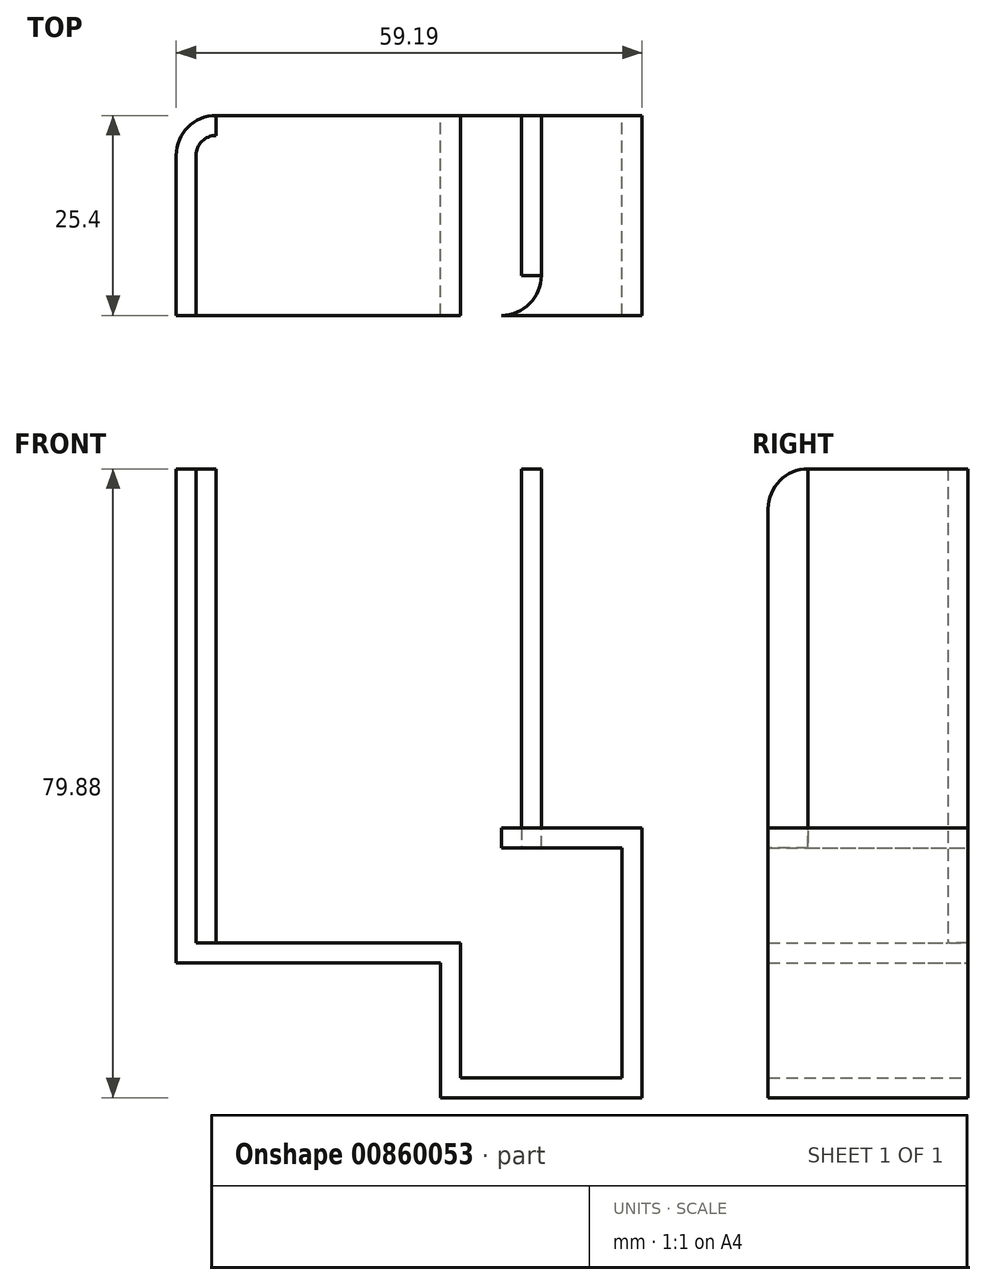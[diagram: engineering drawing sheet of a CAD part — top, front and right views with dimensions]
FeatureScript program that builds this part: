
annotation { "Feature Type Name" : "Feature", "Feature Type Description" : "" }
export const myFeature = defineFeature(function(context is Context, id is Id, definition is map)
    precondition{}
    {
        {
            var Q0;
            Q0=qCreatedBy(makeId("Front.planeOp"),FACE);
            var sketch = newSketch(context, id + "F0", { "sketchPlane" : qUnion([Q0])});
            skLineSegment(sketch, "E0.bottom", {"start": v(-8.21, 15.44) * mm, "end": v(-33.8, 15.44) * mm});
            skLineSegment(sketch, "E0.top", {"start": v(-8.21, -18.82) * mm, "end": v(-33.8, -18.82) * mm});
            skLineSegment(sketch, "E0.left", {"start": v(-8.21, 15.44) * mm, "end": v(-8.21, -18.82) * mm});
            skLineSegment(sketch, "E0.right", {"start": v(-33.8, 15.44) * mm, "end": v(-33.8, -18.82) * mm});
            skPoint(sketch, "E1.firstSnap0", {"position": v(-21, 15.44) * mm});
            skPoint(sketch, "E1.firstSnap1", {"position": v(-8.21, -1.7) * mm});
            skLineSegment(sketch, "E1.bottom", {"start": v(-21, -1.7) * mm, "end": v(-67.4, -1.7) * mm});
            skLineSegment(sketch, "E1.top", {"start": v(-21, 61.06) * mm, "end": v(-67.4, 61.06) * mm});
            skLineSegment(sketch, "E1.left", {"start": v(-21, -1.7) * mm, "end": v(-21, 61.06) * mm});
            skLineSegment(sketch, "E1.right", {"start": v(-67.4, -1.7) * mm, "end": v(-67.4, 61.06) * mm});
            skSolve(sketch);
        }
        {
            var Q0;
            Q0 = qSketchRegion(id + "F0", true);
            extrude(context, id + "F1", {"entities" : qUnion([Q0]), "depth" : 25.4 * mm, "offsetDistance" : 25.4 * mm});
        }
        {
            var Q0;
            Q0=makeQuery(id+"F1.opExtrude","CAP_EDGE",EDGE,{"disambiguationData":[OSD([sQuery(id+"F0.wireOp",EDGE,"E1.right")])],"isStart":true});
            var Q1;
            Q1=makeQuery(id+"F1.opExtrude","CAP_EDGE",EDGE,{"disambiguationData":[OSD([sQuery(id+"F0.wireOp",EDGE,"E1.top")])],"isStart":false});
            var Q2;
            Q2=makeQuery(id+"F1.opExtrude","CAP_EDGE",EDGE,{"disambiguationData":[OSD([sQuery(id+"F0.wireOp",EDGE,"E1.left")])],"isStart":false});
            fillet(context, id + "F2", {"entities" : qUnion([Q0, Q1, Q2]), "radius" : 5.08 * mm, "tangentPropagation" : true, "allowEdgeOverflow" : false});
        }
        {
            var Q0;
            Q0=makeQuery(id+"F1.opExtrude","CAP_FACE",FACE,{"disambiguationData":[OSD([sQuery(id+"F0.wireOp",EDGE,"E0.bottom"),sQuery(id+"F0.wireOp",EDGE,"E0.top"),sQuery(id+"F0.wireOp",EDGE,"E0.left"),sQuery(id+"F0.wireOp",EDGE,"E0.right"),sQuery(id+"F0.wireOp",EDGE,"E1.bottom"),sQuery(id+"F0.wireOp",EDGE,"E1.top"),sQuery(id+"F0.wireOp",EDGE,"E1.left"),sQuery(id+"F0.wireOp",EDGE,"E1.right")])],"isStart":false});
            var Q1;
            Q1=makeQuery(id+"F1.opExtrude","CAP_FACE",FACE,{"disambiguationData":[OSD([sQuery(id+"F0.wireOp",EDGE,"E0.bottom"),sQuery(id+"F0.wireOp",EDGE,"E0.top"),sQuery(id+"F0.wireOp",EDGE,"E0.left"),sQuery(id+"F0.wireOp",EDGE,"E0.right"),sQuery(id+"F0.wireOp",EDGE,"E1.bottom"),sQuery(id+"F0.wireOp",EDGE,"E1.top"),sQuery(id+"F0.wireOp",EDGE,"E1.left"),sQuery(id+"F0.wireOp",EDGE,"E1.right")])],"isStart":true});
            var Q2;
            Q2=makeQuery(id+"F2.opFillet","BLEND_FACE",FACE,{"disambiguationData":[OSD([sQuery(id+"F0.wireOp",EDGE,"E1.top")])]});
            var Q3;
            Q3=makeQuery(id+"F1.opExtrude","SWEPT_FACE",FACE,{"disambiguationData":[OSD([sQuery(id+"F0.wireOp",EDGE,"E1.top")])]});
            var Q4;
            Q4=makeQuery(id+"F2.opFillet","BLEND_FACE",FACE,{"disambiguationData":[OSD([sQuery(id+"F0.wireOp",EDGE,"E1.left")])]});
            shell(context, id + "F3", {"entities" : qUnion([Q0, Q1, Q2, Q3, Q4]), "thickness" : 2.54 * mm});
        }
    });
